# Revit family: E 0360 OPC (2017)
name_source: partatom
category: Lighting Fixtures
revit_build: Autodesk Revit 2017 (Build: 20160225_1515(x64)
units: mm (PartAtom-declared; Revit-internal decimal feet)

## family parameters
Cut with Voids When Loaded = No
Host = Face
Light Source = Yes
Part Type = Normal
Room Calculation Point = No
Round Connector Dimension = Use Diameter
Shared = No

## types (6) — shared parameters
Color Filter = 16777215
Default Elevation = 1219 mm
Dimming Lamp Color Temperature Shift = <None>
Emit Shape Visible in Rendering = No
Emit from Circle Diameter = 360 mm  [stored 1.1811 ft]
Manufacturer = ARLIGHT
Model = E0360OPC
Tilt Angle = 90.00°

## per-type parameters (varying)
| type | Apparent Load | Photometric Web File | Type Comments | Type Image | URL | Wattage Comments |
| EOPC.360.15.30 | 14 VA | E 0360 OPC-15W-3K(SA).IES |  | e0360opc-gorsel.png | arlight.net/urunler/ic-aydinlatma/endustriyel-aydinlatma/e-0360-opc | 15 |
| EOPC.360.15.40 | 14 VA | E 0360 OPC-15W-4K(SA).IES | 15W 4000K | <None> |  | 15 |
| EOPC.360.21.30 | 20 VA | E 0360 OPC-21W-3K(SA).IES | 21W 3K | e0360opc-gorsel.png | arlight.net/urunler/ic-aydinlatma/endustriyel-aydinlatma/e-0360-opc | 21 |
| EOPC.360.21.40 | 20 VA | E 0360 OPC-21W-4K(SA).IES | 21W 4K | e0360opc-gorsel.png | arlight.net/urunler/ic-aydinlatma/endustriyel-aydinlatma/e-0360-opc | 21 |
| EOPC.360.27.30 | 26 VA | E 0360 OPC-27W-3K(SA).IES | 27W 3K | e0360opc-gorsel.png | arlight.net/urunler/ic-aydinlatma/endustriyel-aydinlatma/e-0360-opc | 27 |
| EOPC.360.27.40 | 26 VA | E 0360 OPC-27W-4K(SA).IES | 27W 4K | e0360opc-gorsel.png | arlight.net/urunler/ic-aydinlatma/endustriyel-aydinlatma/e-0360-opc | 27 |

note: [stored X ft] marks values corroborated as IEEE doubles in the binary element streams (Revit-internal decimal feet)

## geometry (parser evidence)
native form markers: Sweep x3
no freeform markers — native parametric forms only
